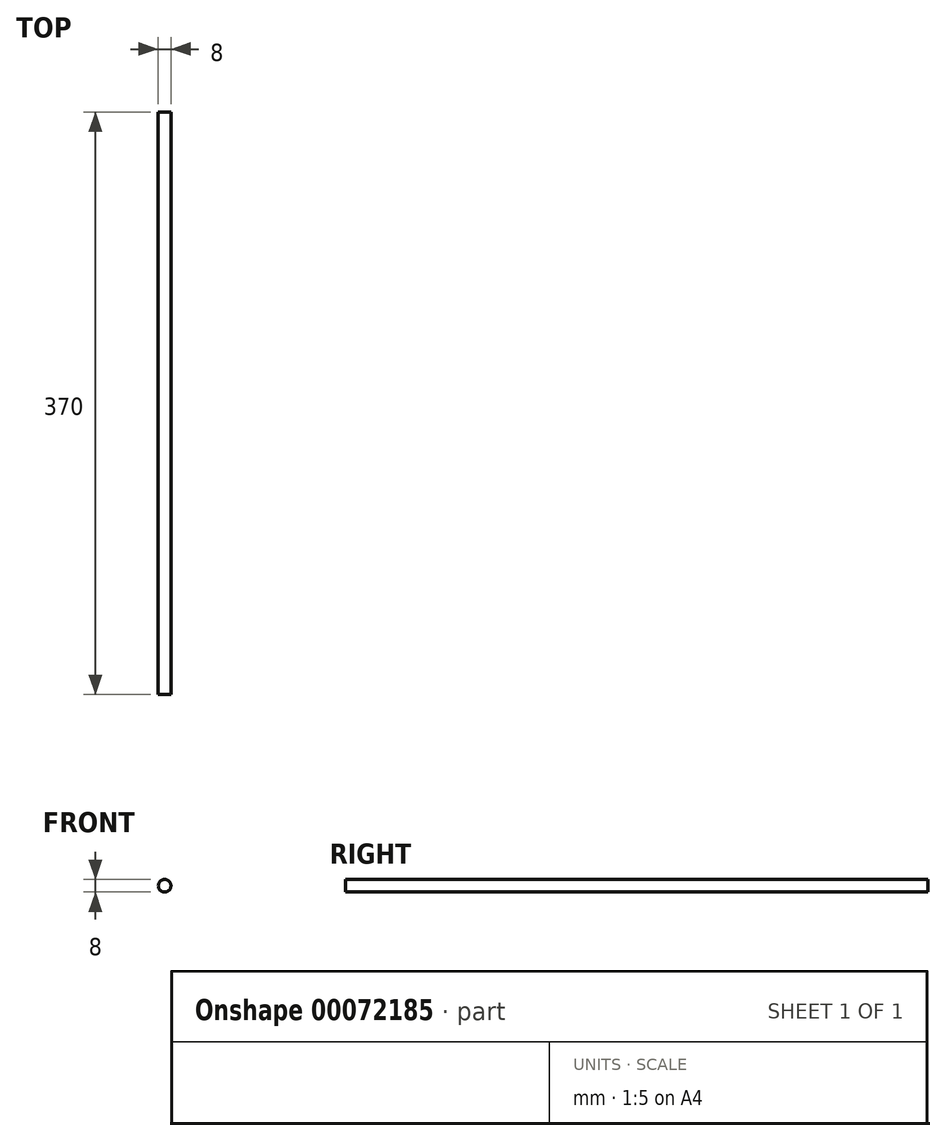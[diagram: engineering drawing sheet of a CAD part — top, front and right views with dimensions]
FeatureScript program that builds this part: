
annotation { "Feature Type Name" : "Feature", "Feature Type Description" : "" }
export const myFeature = defineFeature(function(context is Context, id is Id, definition is map)
    precondition{}
    {
        {
            var Q0;
            Q0=qCreatedBy(makeId("Front.planeOp"),FACE);
            var sketch = newSketch(context, id + "F0", { "sketchPlane" : qUnion([Q0])});
            skCircle(sketch, "E0", {"center": v(0, 0) * mm, "radius": 4 * mm});
            skSolve(sketch);
        }
        {
            var Q0;
            Q0=makeQuery(id+"F0.imprint","IMPRINT",FACE,{"disambiguationData":[TD([[makeQuery(id+"F0.imprint","IMPRINT",EDGE,{"derivedFrom":sQuery(id+"F0.wireOp",EDGE,"E0")}),1.0]])]});
            extrude(context, id + "F1", {"entities" : qUnion([Q0]), "endBound" : BoundingType.SYMMETRIC, "depth" : 370 * mm});
        }
    });
